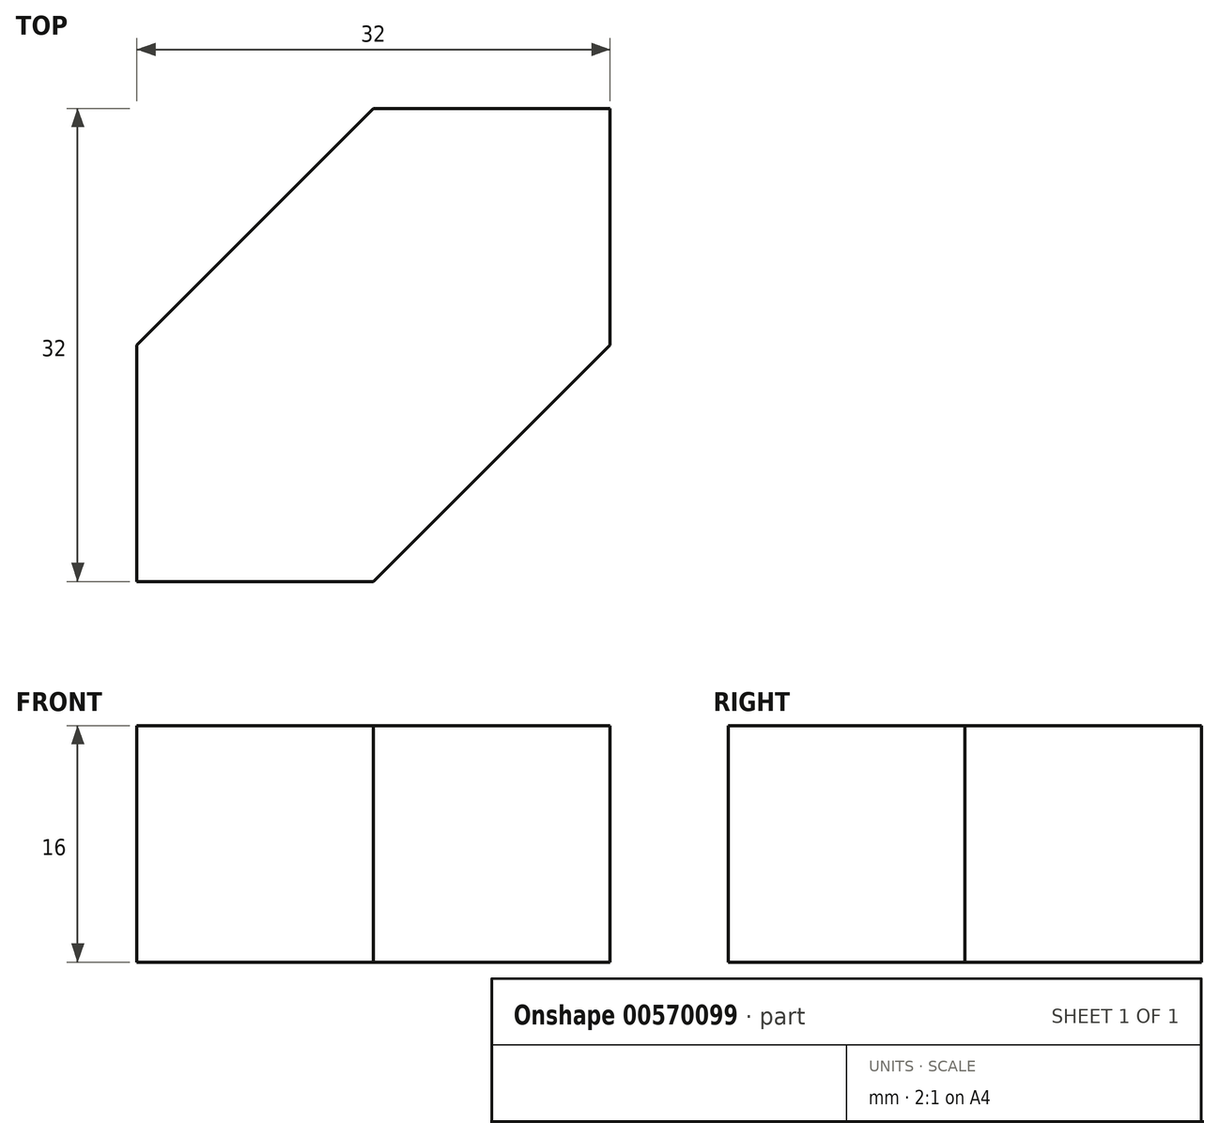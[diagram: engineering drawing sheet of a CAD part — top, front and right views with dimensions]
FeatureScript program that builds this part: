
annotation { "Feature Type Name" : "Feature", "Feature Type Description" : "" }
export const myFeature = defineFeature(function(context is Context, id is Id, definition is map)
    precondition{}
    {
        {
            var Q0;
            Q0=qCreatedBy(makeId("Top.planeOp"),FACE);
            var sketch = newSketch(context, id + "F0", { "sketchPlane" : qUnion([Q0])});
            skLineSegment(sketch, "E0.top", {"start": v(0, -16) * mm, "end": v(-16, -16) * mm});
            skLineSegment(sketch, "E0.right", {"start": v(-16, 0) * mm, "end": v(-16, -16) * mm});
            skLineSegment(sketch, "E1.top", {"start": v(0, 16) * mm, "end": v(16, 16) * mm});
            skLineSegment(sketch, "E1.right", {"start": v(16, 0) * mm, "end": v(16, 16) * mm});
            skLineSegment(sketch, "E2", {"start": v(0, 16) * mm, "end": v(-16, 0) * mm});
            skLineSegment(sketch, "E3", {"start": v(16, 0) * mm, "end": v(0, -16) * mm});
            skSolve(sketch);
        }
        {
            var Q0;
            Q0=makeQuery(id+"F0.imprint","IMPRINT",FACE,{"disambiguationData":[TD([[makeQuery(id+"F0.imprint","IMPRINT",EDGE,{"derivedFrom":sQuery(id+"F0.wireOp",EDGE,"E0.top")}),-1.0]])]});
            extrude(context, id + "F1", {"entities" : qUnion([Q0]), "depth" : 16 * mm, "offsetDistance" : 25.4 * mm});
        }
    });
